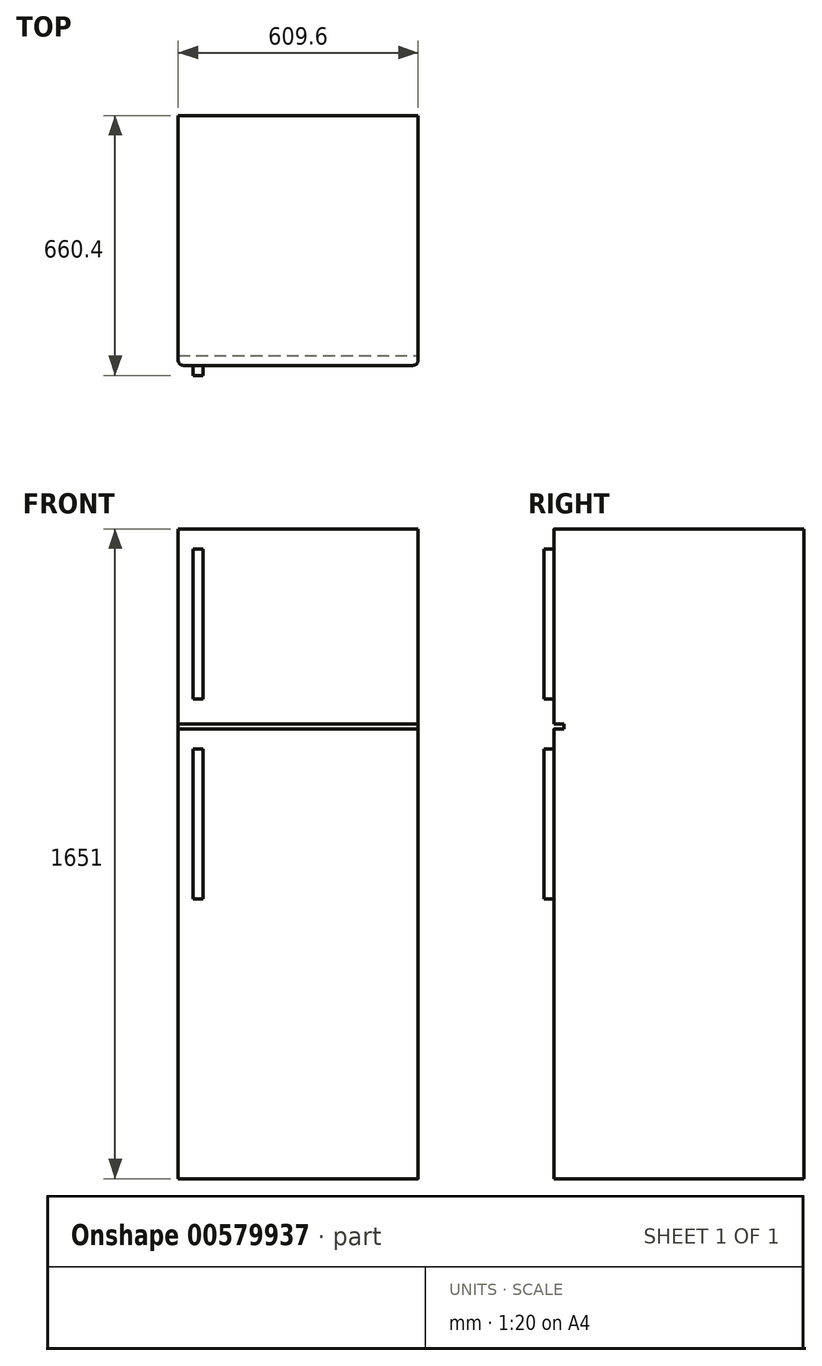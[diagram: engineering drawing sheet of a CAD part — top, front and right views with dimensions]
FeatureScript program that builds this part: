
annotation { "Feature Type Name" : "Feature", "Feature Type Description" : "" }
export const myFeature = defineFeature(function(context is Context, id is Id, definition is map)
    precondition{}
    {
        {
            var Q0;
            Q0=qCreatedBy(makeId("Front.planeOp"),FACE);
            var sketch = newSketch(context, id + "F0", { "sketchPlane" : qUnion([Q0])});
            skLineSegment(sketch, "E0.bottom", {"start": v(-306.7, 1150.28) * mm, "end": v(302.9, 1150.28) * mm});
            skLineSegment(sketch, "E0.top", {"start": v(-306.7, -500.72) * mm, "end": v(302.9, -500.72) * mm});
            skLineSegment(sketch, "E0.left", {"start": v(-306.7, 1150.28) * mm, "end": v(-306.7, -500.72) * mm});
            skLineSegment(sketch, "E0.right", {"start": v(302.9, 1150.28) * mm, "end": v(302.9, -500.72) * mm});
            skSolve(sketch);
        }
        {
            var Q0;
            Q0 = qSketchRegion(id + "F0", true);
            extrude(context, id + "F1", {"entities" : qUnion([Q0]), "depth" : 609.6 * mm, "offsetDistance" : 25.4 * mm});
        }
        {
            var Q0;
            Q0=makeQuery(id+"F1.opExtrude","CAP_FACE",FACE,{"disambiguationData":[OSD([sQuery(id+"F0.wireOp",EDGE,"E0.bottom"),sQuery(id+"F0.wireOp",EDGE,"E0.top"),sQuery(id+"F0.wireOp",EDGE,"E0.left"),sQuery(id+"F0.wireOp",EDGE,"E0.right")])],"isStart":false});
            var sketch = newSketch(context, id + "F2", { "sketchPlane" : qUnion([Q0])});
            skLineSegment(sketch, "E1.bottom", {"start": v(-306.7, -500.72) * mm, "end": v(302.9, -500.72) * mm});
            skLineSegment(sketch, "E1.top", {"start": v(-306.7, 642.28) * mm, "end": v(302.9, 642.28) * mm});
            skLineSegment(sketch, "E1.left", {"start": v(-306.7, -500.72) * mm, "end": v(-306.7, 642.28) * mm});
            skLineSegment(sketch, "E1.right", {"start": v(302.9, -500.72) * mm, "end": v(302.9, 642.28) * mm});
            skLineSegment(sketch, "E2.bottom", {"start": v(-306.7, 1150.28) * mm, "end": v(302.9, 1150.28) * mm});
            skLineSegment(sketch, "E2.top", {"start": v(-306.7, 654.98) * mm, "end": v(302.9, 654.98) * mm});
            skLineSegment(sketch, "E2.left", {"start": v(-306.7, 1150.28) * mm, "end": v(-306.7, 654.98) * mm});
            skLineSegment(sketch, "E2.right", {"start": v(302.9, 1150.28) * mm, "end": v(302.9, 654.98) * mm});
            skSolve(sketch);
        }
        {
            var Q0;
            Q0 = qSketchRegion(id + "F2", true);
            extrude(context, id + "F3", {"entities" : qUnion([Q0]), "operationType" : NewBodyOperationType.ADD, "depth" : 25.4 * mm, "offsetDistance" : 25.4 * mm});
        }
        {
            var Q0;
            Q0=makeQuery(id+"F3.opExtrude","CAP_FACE",FACE,{"disambiguationData":[OSD([sQuery(id+"F2.wireOp",EDGE,"E2.bottom"),sQuery(id+"F2.wireOp",EDGE,"E2.top"),sQuery(id+"F2.wireOp",EDGE,"E2.left"),sQuery(id+"F2.wireOp",EDGE,"E2.right")])],"isStart":false});
            var sketch = newSketch(context, id + "F4", { "sketchPlane" : qUnion([Q0])});
            skLineSegment(sketch, "E3.bottom", {"start": v(-268.6, 1099.48) * mm, "end": v(-243.2, 1099.48) * mm});
            skLineSegment(sketch, "E3.top", {"start": v(-268.6, 718.48) * mm, "end": v(-243.2, 718.48) * mm});
            skLineSegment(sketch, "E3.left", {"start": v(-268.6, 1099.48) * mm, "end": v(-268.6, 718.48) * mm});
            skLineSegment(sketch, "E3.right", {"start": v(-243.2, 1099.48) * mm, "end": v(-243.2, 718.48) * mm});
            skLineSegment(sketch, "E4.bottom", {"start": v(-268.6, 591.48) * mm, "end": v(-243.2, 591.48) * mm});
            skLineSegment(sketch, "E4.top", {"start": v(-268.6, 210.48) * mm, "end": v(-243.2, 210.48) * mm});
            skLineSegment(sketch, "E4.left", {"start": v(-268.6, 591.48) * mm, "end": v(-268.6, 210.48) * mm});
            skLineSegment(sketch, "E4.right", {"start": v(-243.2, 591.48) * mm, "end": v(-243.2, 210.48) * mm});
            skSolve(sketch);
        }
        {
            var Q0;
            Q0 = qSketchRegion(id + "F4", true);
            extrude(context, id + "F5", {"entities" : qUnion([Q0]), "operationType" : NewBodyOperationType.ADD, "depth" : 25.4 * mm, "offsetDistance" : 25.4 * mm});
        }
        {
            var Q0;
            Q0=makeQuery(id+"F3.opExtrude","CAP_EDGE",EDGE,{"disambiguationData":[OSD([sQuery(id+"F2.wireOp",EDGE,"E2.right")])],"isStart":false});
            var Q1;
            Q1=makeQuery(id+"F3.opExtrude","CAP_EDGE",EDGE,{"disambiguationData":[OSD([sQuery(id+"F2.wireOp",EDGE,"E1.right")])],"isStart":false});
            var Q2;
            Q2=makeQuery(id+"F3.opExtrude","CAP_EDGE",EDGE,{"disambiguationData":[OSD([sQuery(id+"F2.wireOp",EDGE,"E2.left")])],"isStart":false});
            var Q3;
            Q3=makeQuery(id+"F3.opExtrude","CAP_EDGE",EDGE,{"disambiguationData":[OSD([sQuery(id+"F2.wireOp",EDGE,"E1.left")])],"isStart":false});
            fillet(context, id + "F6", {"entities" : qUnion([Q0, Q1, Q2, Q3]), "radius" : 12.7 * mm, "tangentPropagation" : true, "allowEdgeOverflow" : false});
        }
    });
